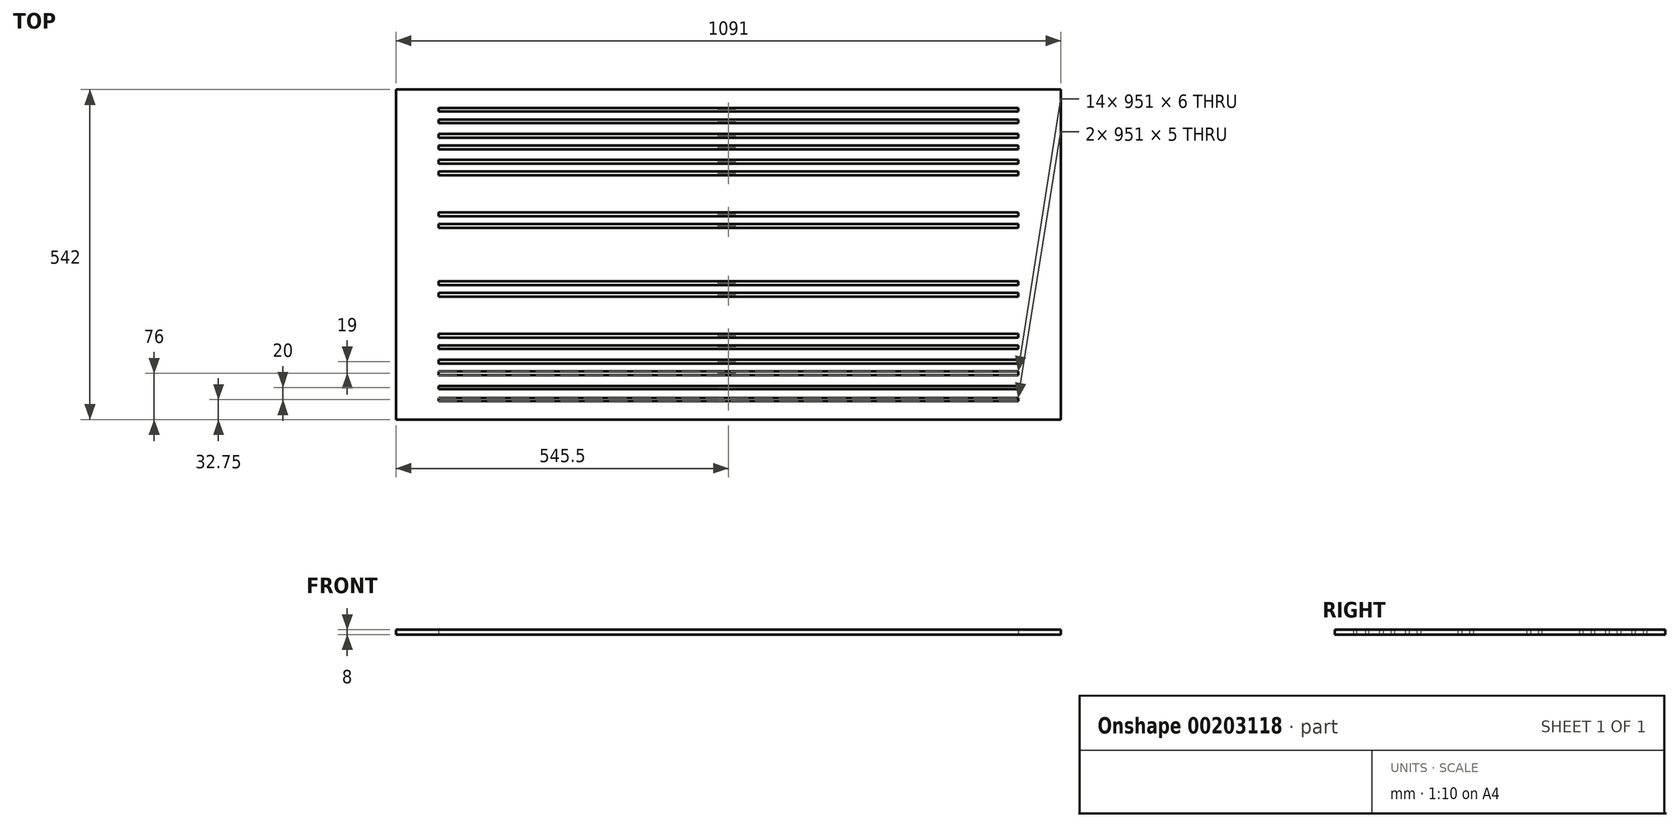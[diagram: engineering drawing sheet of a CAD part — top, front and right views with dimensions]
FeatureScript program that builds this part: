
annotation { "Feature Type Name" : "Feature", "Feature Type Description" : "" }
export const myFeature = defineFeature(function(context is Context, id is Id, definition is map)
    precondition{}
    {
        {
            var Q0;
            Q0=qCreatedBy(makeId("Top.planeOp"),FACE);
            var sketch = newSketch(context, id + "F0", { "sketchPlane" : qUnion([Q0])});
            skLineSegment(sketch, "E0.bottom", {"start": v(0, 0) * mm, "end": v(1091, 0) * mm});
            skLineSegment(sketch, "E0.top", {"start": v(0, 542) * mm, "end": v(1091, 542) * mm});
            skLineSegment(sketch, "E0.left", {"start": v(0, 0) * mm, "end": v(0, 542) * mm});
            skLineSegment(sketch, "E0.right", {"start": v(1091, 0) * mm, "end": v(1091, 542) * mm});
            skPoint(sketch, "E1", {"position": v(214, 171) * mm});
            skPoint(sketch, "E2", {"position": v(214, 271) * mm});
            skPoint(sketch, "E3", {"position": v(214, 371) * mm});
            skLineSegment(sketch, "E4", {"start": v(-315.3, 371) * mm, "end": v(-315.3, 271) * mm, "construction": true});
            skLineSegment(sketch, "E5", {"start": v(-315.3, 271) * mm, "end": v(-315.3, 171) * mm, "construction": true});
            skLineSegment(sketch, "E6", {"start": v(-315.3, 171) * mm, "end": v(-315.3, 0) * mm, "construction": true});
            skLineSegment(sketch, "E7", {"start": v(-315.3, 542) * mm, "end": v(-315.3, 371) * mm, "construction": true});
            skPoint(sketch, "E8", {"position": v(-315.3, 456.5) * mm});
            skPoint(sketch, "E9", {"position": v(-315.3, 327.44) * mm});
            skPoint(sketch, "E10", {"position": v(-315.3, 221) * mm});
            skPoint(sketch, "E11", {"position": v(-315.3, 85.5) * mm});
            skLineSegment(sketch, "E12", {"start": v(50, 327.44) * mm, "end": v(1041, 327.44) * mm, "construction": true});
            skLineSegment(sketch, "E13", {"start": v(50, 456.5) * mm, "end": v(1041, 456.5) * mm, "construction": true});
            skLineSegment(sketch, "E14", {"start": v(1046.67, 271) * mm, "end": v(1429.51, 271) * mm, "construction": true});
            skPoint(sketch, "E14.endSnap0", {"position": v(1091, 271) * mm});
            skLineSegment(sketch, "E15", {"start": v(-218.04, 542) * mm, "end": v(-218.04, 456.5) * mm, "construction": true});
            skPoint(sketch, "E16", {"position": v(-218.04, 499.25) * mm});
            skLineSegment(sketch, "E17", {"start": v(50, 499.25) * mm, "end": v(1041, 499.25) * mm, "construction": true});
            skLineSegment(sketch, "E18", {"start": v(-218.04, 456.5) * mm, "end": v(-218.04, 371) * mm, "construction": true});
            skPoint(sketch, "E19", {"position": v(-218.04, 413.75) * mm});
            skLineSegment(sketch, "E20", {"start": v(50, 413.75) * mm, "end": v(1041, 413.75) * mm, "construction": true});
            skLineSegment(sketch, "E21.MirrorCS", {"start": v(50, 42.75) * mm, "end": v(1041, 42.75) * mm, "construction": true});
            skLineSegment(sketch, "E22.MirrorCS", {"start": v(50, 85.5) * mm, "end": v(1041, 85.5) * mm, "construction": true});
            skLineSegment(sketch, "E23.MirrorCS", {"start": v(50, 128.25) * mm, "end": v(1041, 128.25) * mm, "construction": true});
            skLineSegment(sketch, "E24.MirrorCS", {"start": v(50, 214.56) * mm, "end": v(1041, 214.56) * mm, "construction": true});
            skSolve(sketch);
        }
        {
            var Q0;
            Q0=makeQuery(id+"F0.imprint","IMPRINT",FACE,{"disambiguationData":[TD([[makeQuery(id+"F0.imprint","IMPRINT",EDGE,{"derivedFrom":sQuery(id+"F0.wireOp",EDGE,"E0.bottom")}),1.0]])]});
            var sketch = newSketch(context, id + "F1", { "sketchPlane" : qUnion([Q0])});
            skLineSegment(sketch, "E25.bottom", {"start": v(0, 0) * mm, "end": v(1091, 0) * mm});
            skLineSegment(sketch, "E25.top", {"start": v(0, 542) * mm, "end": v(1091, 542) * mm});
            skLineSegment(sketch, "E25.left", {"start": v(0, 0) * mm, "end": v(0, 542) * mm});
            skLineSegment(sketch, "E25.right", {"start": v(1091, 0) * mm, "end": v(1091, 542) * mm});
            skLineSegment(sketch, "E26.JFx.JFx", {"start": v(50, 499.25) * mm, "end": v(1041, 499.25) * mm, "construction": true});
            skLineSegment(sketch, "E26.JFl.JFl", {"start": v(50, 456.5) * mm, "end": v(1041, 456.5) * mm, "construction": true});
            skLineSegment(sketch, "E26.JF5.JF5", {"start": v(50, 413.75) * mm, "end": v(1041, 413.75) * mm, "construction": true});
            skLineSegment(sketch, "E26.JFh.JFh", {"start": v(50, 327.44) * mm, "end": v(1041, 327.44) * mm, "construction": true});
            skLineSegment(sketch, "E26.KFJB.KFJB", {"start": v(50, 214.56) * mm, "end": v(1041, 214.56) * mm, "construction": true});
            skLineSegment(sketch, "E26.KFFB.KFFB", {"start": v(50, 128.25) * mm, "end": v(1041, 128.25) * mm, "construction": true});
            skLineSegment(sketch, "E26.KFBB.KFBB", {"start": v(50, 85.5) * mm, "end": v(1041, 85.5) * mm, "construction": true});
            skLineSegment(sketch, "E26.JF9.JF9", {"start": v(50, 42.75) * mm, "end": v(1041, 42.75) * mm, "construction": true});
            skLineSegment(sketch, "E26.0.left", {"start": v(70, 511.75) * mm, "end": v(1021, 511.75) * mm});
            skLineSegment(sketch, "E26.0.right", {"start": v(70, 486.75) * mm, "end": v(1021, 486.75) * mm});
            skLineSegment(sketch, "E26.1.left", {"start": v(70, 469) * mm, "end": v(1041, 469) * mm});
            skLineSegment(sketch, "E26.1.right", {"start": v(70, 444) * mm, "end": v(1021, 444) * mm});
            skLineSegment(sketch, "E26.2.left", {"start": v(70, 426.25) * mm, "end": v(1021, 426.25) * mm});
            skLineSegment(sketch, "E26.2.right", {"start": v(70, 401.25) * mm, "end": v(1021, 401.25) * mm});
            skLineSegment(sketch, "E26.3.left", {"start": v(70, 339.94) * mm, "end": v(1021, 339.94) * mm});
            skLineSegment(sketch, "E26.3.right", {"start": v(70, 314.94) * mm, "end": v(1021, 314.94) * mm});
            skLineSegment(sketch, "E26.4.left", {"start": v(70, 227.06) * mm, "end": v(1021, 227.06) * mm});
            skLineSegment(sketch, "E26.4.right", {"start": v(70, 202.06) * mm, "end": v(1041, 202.06) * mm});
            skLineSegment(sketch, "E26.5.left", {"start": v(70, 140.75) * mm, "end": v(1021, 140.75) * mm});
            skLineSegment(sketch, "E26.5.right", {"start": v(70, 115.75) * mm, "end": v(1021, 115.75) * mm});
            skLineSegment(sketch, "E26.6.left", {"start": v(70, 98) * mm, "end": v(1021, 98) * mm});
            skLineSegment(sketch, "E26.6.right", {"start": v(70, 73) * mm, "end": v(1021, 73) * mm});
            skLineSegment(sketch, "E26.7.left", {"start": v(70, 55.25) * mm, "end": v(1021, 55.25) * mm});
            skLineSegment(sketch, "E26.7.right", {"start": v(70, 30.25) * mm, "end": v(1021, 30.25) * mm});
            skPoint(sketch, "E27", {"position": v(545.5, 511.75) * mm});
            skLineSegment(sketch, "E28.top", {"start": v(70, 505.75) * mm, "end": v(1021, 505.75) * mm});
            skLineSegment(sketch, "E28.left", {"start": v(70, 511.75) * mm, "end": v(70, 505.75) * mm});
            skLineSegment(sketch, "E28.right", {"start": v(1021, 511.75) * mm, "end": v(1021, 505.75) * mm});
            skLineSegment(sketch, "E29.bottom", {"start": v(70, 492.75) * mm, "end": v(1021, 492.75) * mm});
            skLineSegment(sketch, "E29.left", {"start": v(70, 492.75) * mm, "end": v(70, 486.75) * mm});
            skLineSegment(sketch, "E29.right", {"start": v(1021, 492.75) * mm, "end": v(1021, 486.75) * mm});
            skLineSegment(sketch, "E30.top", {"start": v(70, 92) * mm, "end": v(1021, 92) * mm});
            skLineSegment(sketch, "E30.left", {"start": v(1021, 98) * mm, "end": v(1021, 92) * mm});
            skLineSegment(sketch, "E30.right", {"start": v(70, 98) * mm, "end": v(70, 92) * mm});
            skPoint(sketch, "E31", {"position": v(545.5, 98) * mm});
            skLineSegment(sketch, "E32.bottom", {"start": v(70, 79) * mm, "end": v(1021, 79) * mm});
            skLineSegment(sketch, "E32.left", {"start": v(1021, 79) * mm, "end": v(1021, 73) * mm});
            skLineSegment(sketch, "E32.right", {"start": v(70, 79) * mm, "end": v(70, 73) * mm});
            skLineSegment(sketch, "E33.top", {"start": v(70, 420.25) * mm, "end": v(1021, 420.25) * mm});
            skLineSegment(sketch, "E33.left", {"start": v(1021, 426.25) * mm, "end": v(1021, 420.25) * mm});
            skLineSegment(sketch, "E33.right", {"start": v(70, 426.25) * mm, "end": v(70, 420.25) * mm});
            skPoint(sketch, "E34", {"position": v(545.5, 426.25) * mm});
            skLineSegment(sketch, "E35.bottom", {"start": v(70, 407.25) * mm, "end": v(1021, 407.25) * mm});
            skLineSegment(sketch, "E35.left", {"start": v(1021, 407.25) * mm, "end": v(1021, 401.25) * mm});
            skLineSegment(sketch, "E35.right", {"start": v(70, 407.25) * mm, "end": v(70, 401.25) * mm});
            skLineSegment(sketch, "E36.bottom", {"start": v(70, 469) * mm, "end": v(1021, 469) * mm});
            skLineSegment(sketch, "E36.top", {"start": v(70, 463) * mm, "end": v(1021, 463) * mm});
            skLineSegment(sketch, "E36.left", {"start": v(1021, 469) * mm, "end": v(1021, 463) * mm});
            skLineSegment(sketch, "E36.right", {"start": v(70, 469) * mm, "end": v(70, 463) * mm});
            skPoint(sketch, "E37", {"position": v(545.5, 469) * mm});
            skLineSegment(sketch, "E38.bottom", {"start": v(70, 450) * mm, "end": v(1021, 450) * mm});
            skLineSegment(sketch, "E38.left", {"start": v(1021, 450) * mm, "end": v(1021, 444) * mm});
            skLineSegment(sketch, "E38.right", {"start": v(70, 450) * mm, "end": v(70, 444) * mm});
            skPoint(sketch, "E39", {"position": v(545.5, 339.94) * mm});
            skPoint(sketch, "E40", {"position": v(545.5, 227.06) * mm});
            skPoint(sketch, "E41", {"position": v(545.5, 140.75) * mm});
            skPoint(sketch, "E42", {"position": v(545.5, 55.25) * mm});
            skLineSegment(sketch, "E43.top", {"start": v(70, 134.75) * mm, "end": v(1021, 134.75) * mm});
            skLineSegment(sketch, "E43.left", {"start": v(70, 140.75) * mm, "end": v(70, 134.75) * mm});
            skLineSegment(sketch, "E43.right", {"start": v(1021, 140.75) * mm, "end": v(1021, 134.75) * mm});
            skLineSegment(sketch, "E44.bottom", {"start": v(70, 121.75) * mm, "end": v(1021, 121.75) * mm});
            skLineSegment(sketch, "E44.left", {"start": v(70, 121.75) * mm, "end": v(70, 115.75) * mm});
            skLineSegment(sketch, "E44.right", {"start": v(1021, 121.75) * mm, "end": v(1021, 115.75) * mm});
            skLineSegment(sketch, "E45.top", {"start": v(70, 50.25) * mm, "end": v(1021, 50.25) * mm});
            skLineSegment(sketch, "E45.left", {"start": v(70, 55.25) * mm, "end": v(70, 50.25) * mm});
            skLineSegment(sketch, "E45.right", {"start": v(1021, 55.25) * mm, "end": v(1021, 50.25) * mm});
            skLineSegment(sketch, "E46.bottom", {"start": v(70, 35.25) * mm, "end": v(1021, 35.25) * mm});
            skLineSegment(sketch, "E46.left", {"start": v(70, 35.25) * mm, "end": v(70, 30.25) * mm});
            skLineSegment(sketch, "E46.right", {"start": v(1021, 35.25) * mm, "end": v(1021, 30.25) * mm});
            skLineSegment(sketch, "E47.top", {"start": v(70, 221.06) * mm, "end": v(1021, 221.06) * mm});
            skLineSegment(sketch, "E47.left", {"start": v(70, 227.06) * mm, "end": v(70, 221.06) * mm});
            skLineSegment(sketch, "E47.right", {"start": v(1021, 227.06) * mm, "end": v(1021, 221.06) * mm});
            skLineSegment(sketch, "E48.bottom", {"start": v(70, 208.06) * mm, "end": v(1021, 208.06) * mm});
            skLineSegment(sketch, "E48.top", {"start": v(70, 202.06) * mm, "end": v(1021, 202.06) * mm});
            skLineSegment(sketch, "E48.left", {"start": v(70, 208.06) * mm, "end": v(70, 202.06) * mm});
            skLineSegment(sketch, "E48.right", {"start": v(1021, 208.06) * mm, "end": v(1021, 202.06) * mm});
            skPoint(sketch, "E49", {"position": v(545.5, 30.25) * mm});
            skLineSegment(sketch, "E50.top", {"start": v(70, 333.94) * mm, "end": v(1021, 333.94) * mm});
            skLineSegment(sketch, "E50.left", {"start": v(70, 339.94) * mm, "end": v(70, 333.94) * mm});
            skLineSegment(sketch, "E50.right", {"start": v(1021, 339.94) * mm, "end": v(1021, 333.94) * mm});
            skLineSegment(sketch, "E51.bottom", {"start": v(70, 320.94) * mm, "end": v(1021, 320.94) * mm});
            skLineSegment(sketch, "E51.left", {"start": v(70, 320.94) * mm, "end": v(70, 314.94) * mm});
            skLineSegment(sketch, "E51.right", {"start": v(1021, 320.94) * mm, "end": v(1021, 314.94) * mm});
            skPoint(sketch, "E52", {"position": v(545.5, 214.56) * mm});
            skPoint(sketch, "E26.7.startCap.end.orphan", {"position": v(50, 55.25) * mm});
            skPoint(sketch, "E26.6.startCap.end.orphan", {"position": v(50, 98) * mm});
            skPoint(sketch, "E26.7.endCap.start.orphan", {"position": v(1041, 55.25) * mm});
            skPoint(sketch, "E53.orphan", {"position": v(1041, 140.75) * mm});
            skPoint(sketch, "E54.orphan", {"position": v(1041, 444) * mm});
            skPoint(sketch, "E55.orphan", {"position": v(1041, 426.25) * mm});
            skPoint(sketch, "E56.orphan", {"position": v(1041, 511.75) * mm});
            skPoint(sketch, "E26.0.startCap.end.orphan", {"position": v(50, 511.75) * mm});
            skPoint(sketch, "E26.1.startCap.end.orphan", {"position": v(50, 469) * mm});
            skPoint(sketch, "E26.2.startCap.end.orphan", {"position": v(50, 426.25) * mm});
            skPoint(sketch, "E26.3.startCap.end.orphan", {"position": v(50, 339.94) * mm});
            skPoint(sketch, "E26.4.startCap.end.orphan", {"position": v(50, 227.06) * mm});
            skPoint(sketch, "E26.5.startCap.end.orphan", {"position": v(50, 140.75) * mm});
            skPoint(sketch, "E57.orphan", {"position": v(1041, 98) * mm});
            skPoint(sketch, "E58.orphan", {"position": v(1041, 227.06) * mm});
            skPoint(sketch, "E59.orphan", {"position": v(1041, 339.94) * mm});
            skSolve(sketch);
        }
        {
            var Q0;
            Q0=makeQuery(id+"F1.imprint","IMPRINT",FACE,{"disambiguationData":[TD([[makeQuery(id+"F1.imprint","IMPRINT",EDGE,{"derivedFrom":sQuery(id+"F1.wireOp",EDGE,"E25.bottom")}),1.0]])]});
            extrude(context, id + "F2", {"entities" : qUnion([Q0]), "depth" : 8 * mm});
        }
    });
